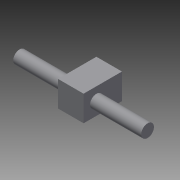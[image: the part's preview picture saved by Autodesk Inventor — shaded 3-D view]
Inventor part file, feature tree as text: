
AUTODESK INVENTOR PART (.ipt)
format: ipt  version: 2014 SP1 (Build 180222100, 222)  size: 82,944 bytes
history: native  units: in
note: dims shown in document units (in); Inventor stores cm internally (conversion verified against a paired STEP export)
features: extrude x2, sketch x2
ambient origin geometry x8: Origin, YZ Plane, XZ Plane, XY Plane, X Axis, Y Axis, Z Axis, Center Point
bodies: Solid1 (feature_tree)
feature tree (4):
  extrude  "Extrusion1"  Depth=1.0in
  extrude  "Extrusion2"  Depth=3.0in
  sketch  "Sketch1"  dims[d0=1.5in d1=1.0in]
  sketch  "Sketch2"  dims[d5=1.0in d6=0.0in d7=0.5in d8=0.5in d9=1.0in d10=2.0in d11=3.0in d12=0.0in d13=0.0in]
